# Revit family: CADS_Vent-Axia_MechEquip_Fan_MFQ_SqrMixedFlow - SUPPLY
name_source: partatom
category: Mechanical Equipment
units: mm (PartAtom-declared; Revit-internal decimal feet)

## family parameters
Always vertical = Yes
Cut with Voids When Loaded = No
OmniClass Number = 23.75.00.00
OmniClass Title = Climate Control (HVAC)
Part Type = Normal
Room Calculation Point = No
Round Connector Dimension = Use Diameter
Shared = No
Work Plane-Based = No

## types (8) — shared parameters
AirflowRateRange = 0.0 L/s
AssemblyPlace = UNKNOWN
AssetType = FIXED
DurationUnit = Year
ExteriorInsulation = No
Fitting Type = Ignore
GrossWeight = 0.00 kg
HasProtectiveEarth = No
IfcExportAs = IfcFanType
IsExtendedWarranty = No
ManufacturerAddress = Fleming Way
Crawley 
RH10 9YX
ModelReference = SQUARE MIXED FLOW FAN
Quantity = 1
RatedCurrent = 0 A
RatedVoltage = 0 V
Status = New
WarrantyGuarantor = Vent-Axia Limited
WorkingPressure = 0.0 Pa
zero-valued in all types: CADS_Index, CADS_Usage, Default Elevation, ExpectedServiceLife, NumberOfPoles

## per-type parameters (varying)
| type | NominalDiameter | NominalHeight | NominalLength | NominalWidth |
| MFQ35014 | 350 mm  [stored 1.14829 ft] | 450 mm  [stored 1.47638 ft] | 400 mm  [stored 1.31234 ft] | 450 mm  [stored 1.47638 ft] |
| MFQ40014 | 400 mm  [stored 1.31234 ft] | 500 mm  [stored 1.64042 ft] | 450 mm  [stored 1.47638 ft] | 500 mm  [stored 1.64042 ft] |
| MFQ40034 | 400 mm  [stored 1.31234 ft] | 500 mm  [stored 1.64042 ft] | 450 mm  [stored 1.47638 ft] | 500 mm  [stored 1.64042 ft] |
| MFQ45014 | 450 mm  [stored 1.47638 ft] | 550 mm | 485 mm  [stored 1.59121 ft] | 550 mm |
| MFQ45034 | 450 mm  [stored 1.47638 ft] | 550 mm | 485 mm  [stored 1.59121 ft] | 550 mm |
| MFQ50014 | 500 mm  [stored 1.64042 ft] | 650 mm  [stored 2.13255 ft] | 510 mm  [stored 1.67323 ft] | 650 mm  [stored 2.13255 ft] |
| MFQ50034 | 500 mm  [stored 1.64042 ft] | 650 mm  [stored 2.13255 ft] | 510 mm  [stored 1.67323 ft] | 650 mm  [stored 2.13255 ft] |
| MFQ56034 | 560 mm  [stored 1.83727 ft] | 700 mm  [stored 2.29659 ft] | 530 mm  [stored 1.73885 ft] | 700 mm  [stored 2.29659 ft] |

note: column(s) folded — value = type name in every type: ModelNumber

note: [stored X ft] marks values corroborated as IEEE doubles in the binary element streams (Revit-internal decimal feet)

## geometry (parser evidence)
native form markers: Sweep x4
no freeform markers — native parametric forms only
